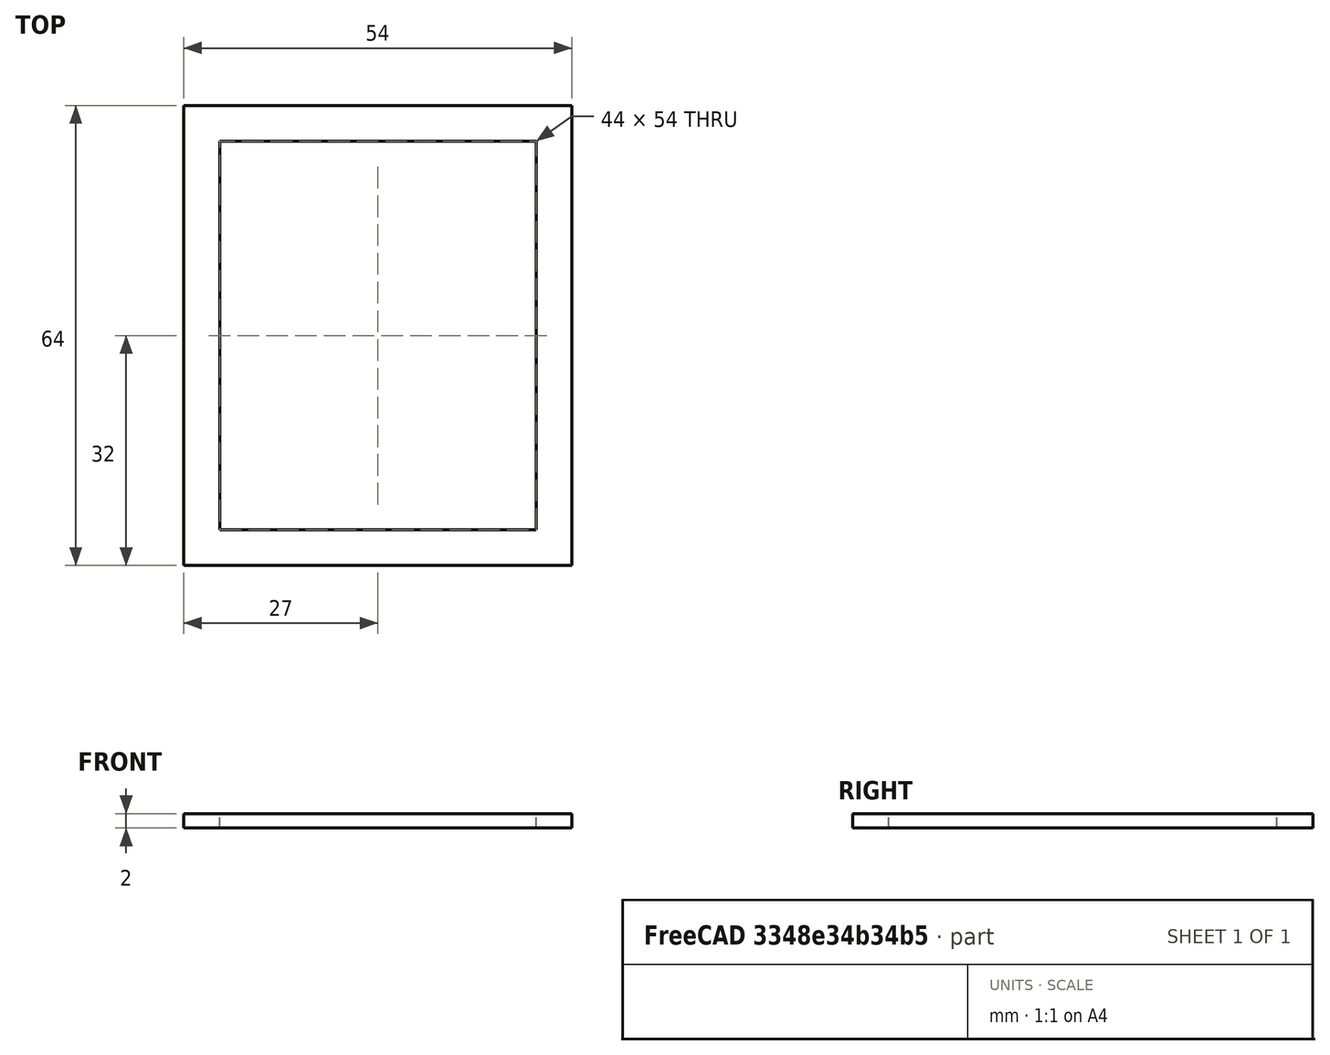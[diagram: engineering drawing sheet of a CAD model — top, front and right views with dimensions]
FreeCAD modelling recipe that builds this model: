
FCSTD DOCUMENT  (FreeCAD 0.16R6706 (Git))
Label: iROB-EA_Modulo_Meteorologia_Tapa_Marco
License: All rights reserved
LicenseURL: http://en.wikipedia.org/wiki/All_rights_reserved
objects: Sketcher::SketchObject×1, PartDesign::Pad×1
note: 3 computed .brp shape members not serialized (recipe doc carries the construction recipe); baked Part::Feature solids carry a one-line shape summary decoded from their .brp

FEATURE [Sketcher::SketchObject] Sketch  label="Marco"
  sketch-geometry (8):
    g0: LineSegment StartX=0 StartY=64 StartZ=0 EndX=54 EndY=64 EndZ=0
    g1: LineSegment StartX=54 StartY=64 StartZ=0 EndX=54 EndY=0 EndZ=0
    g2: LineSegment StartX=54 StartY=0 StartZ=0 EndX=0 EndY=0 EndZ=0
    g3: LineSegment StartX=0 StartY=0 StartZ=0 EndX=0 EndY=64 EndZ=0
    g4: LineSegment StartX=5 StartY=59 StartZ=0 EndX=49 EndY=59 EndZ=0
    g5: LineSegment StartX=49 StartY=59 StartZ=0 EndX=49 EndY=5 EndZ=0
    g6: LineSegment StartX=49 StartY=5 StartZ=0 EndX=5 EndY=5 EndZ=0
    g7: LineSegment StartX=5 StartY=5 StartZ=0 EndX=5 EndY=59 EndZ=0
  constraints (23):
    c: Coincident(g0,g1)
    c: Coincident(g1,g2)
    c: Coincident(g2,g3)
    c: Coincident(g3,g0)
    c: Horizontal(g0)
    c: Horizontal(g2)
    c: Vertical(g1)
    c: Vertical(g3)
    c: DistanceX(g0,g0) = 54
    c: DistanceY(g3,g3) = 64
    c: Coincident(g2,g-1)
    c: Coincident(g4,g5)
    c: Coincident(g5,g6)
    c: Coincident(g6,g7)
    c: Coincident(g7,g4)
    c: Horizontal(g4)
    c: Horizontal(g6)
    c: Vertical(g5)
    c: Vertical(g7)
    c: DistanceX(g4,g4) = 44
    c: DistanceY(g7,g7) = 54
    c: DistanceX(g6,g-1) = -5
    c: DistanceY(g6,g-1) = -5
FEATURE [PartDesign::Pad] Pad
  Length = 2
  Length2 = 100
  Sketch = -> Sketch
  Type = 0
